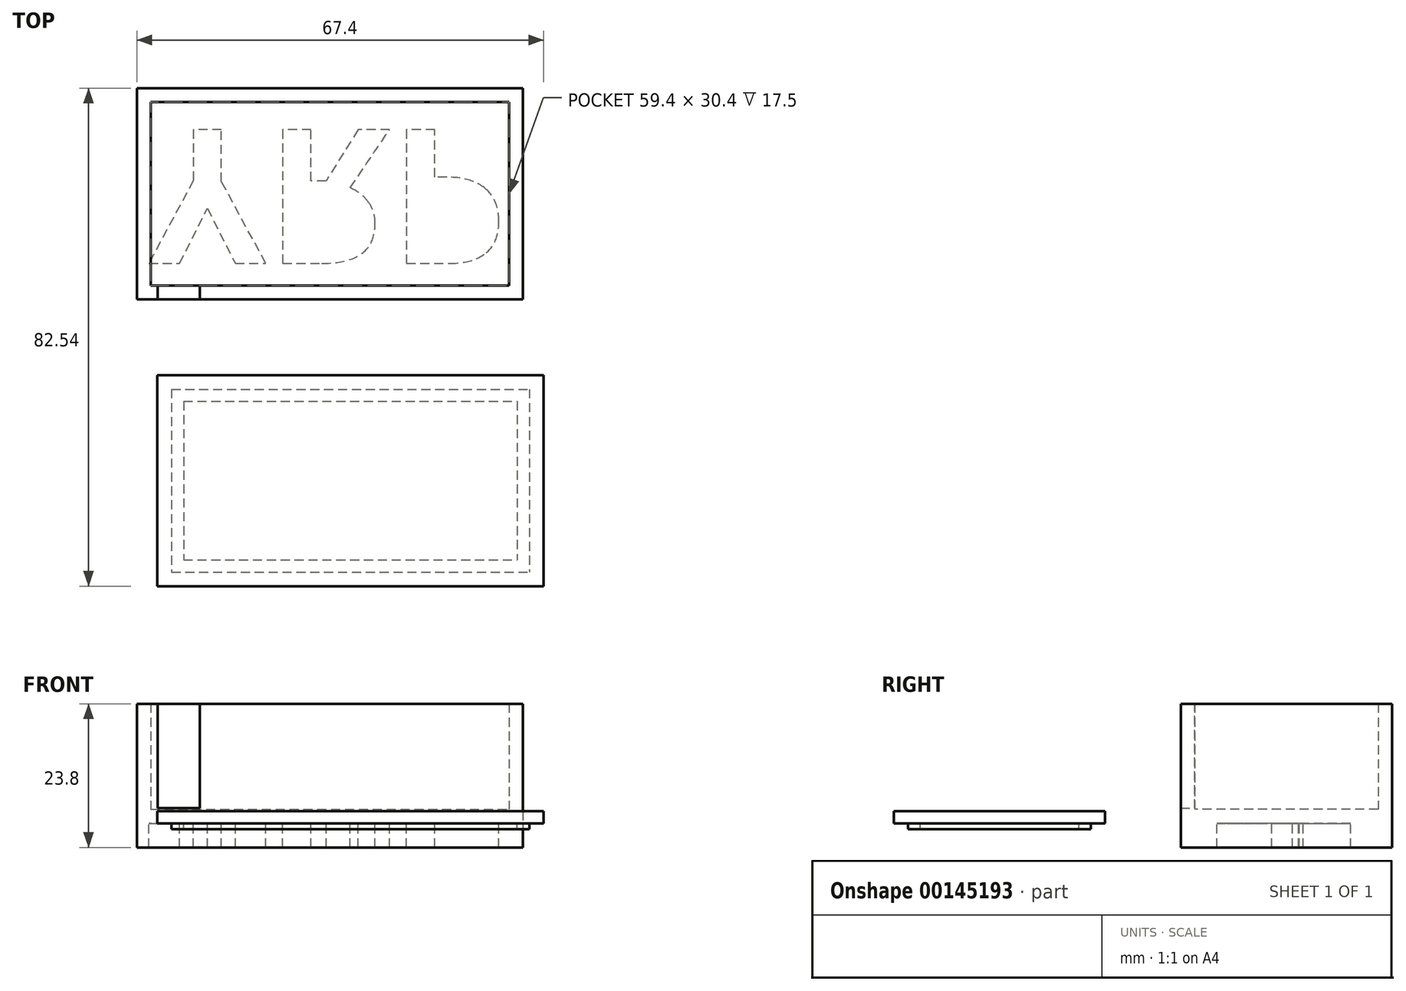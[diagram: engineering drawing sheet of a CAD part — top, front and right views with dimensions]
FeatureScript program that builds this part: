
annotation { "Feature Type Name" : "Feature", "Feature Type Description" : "" }
export const myFeature = defineFeature(function(context is Context, id is Id, definition is map)
    precondition{}
    {
        {
            var Q0;
            Q0=qCreatedBy(makeId("Top.planeOp"),FACE);
            var sketch = newSketch(context, id + "F0", { "sketchPlane" : qUnion([Q0])});
            skLineSegment(sketch, "E0.bottom", {"start": v(-34.01, 10.7) * mm, "end": v(29.99, 10.7) * mm});
            skLineSegment(sketch, "E0.top", {"start": v(-34.01, -24.3) * mm, "end": v(29.99, -24.3) * mm});
            skLineSegment(sketch, "E0.left", {"start": v(-34.01, 10.7) * mm, "end": v(-34.01, -24.3) * mm});
            skLineSegment(sketch, "E0.right", {"start": v(29.99, 10.7) * mm, "end": v(29.99, -24.3) * mm});
            skSolve(sketch);
        }
        {
            var Q0;
            Q0=makeQuery(id+"F0.imprint","IMPRINT",FACE,{"disambiguationData":[TD([[makeQuery(id+"F0.imprint","IMPRINT",EDGE,{"derivedFrom":sQuery(id+"F0.wireOp",EDGE,"E0.bottom")}),-1.0]])]});
            extrude(context, id + "F1", {"entities" : qUnion([Q0]), "depth" : 19.8 * mm});
        }
        {
            var Q0;
            Q0=makeQuery(id+"F1.opExtrude","CAP_FACE",FACE,{"disambiguationData":[OSD([sQuery(id+"F0.wireOp",EDGE,"E0.bottom"),sQuery(id+"F0.wireOp",EDGE,"E0.top"),sQuery(id+"F0.wireOp",EDGE,"E0.left"),sQuery(id+"F0.wireOp",EDGE,"E0.right")])],"isStart":false});
            shell(context, id + "F2", {"entities" : qUnion([Q0]), "thickness" : 2.3 * mm});
        }
        {
            var Q0;
            Q0=makeQuery(id+"F1.opExtrude","CAP_FACE",FACE,{"disambiguationData":[OSD([sQuery(id+"F0.wireOp",EDGE,"E0.bottom"),sQuery(id+"F0.wireOp",EDGE,"E0.top"),sQuery(id+"F0.wireOp",EDGE,"E0.left"),sQuery(id+"F0.wireOp",EDGE,"E0.right")])],"isStart":true});
            var sketch = newSketch(context, id + "F3", { "sketchPlane" : qUnion([Q0])});
            skText(sketch, "E1", { "text": "YRP", "fontName": "OpenSans-Bold.ttf"});
            const initialGuessF3  = {"E1": [-0.03201, -0.00384, 1, 0, 0.02236]};
            skSetInitialGuess(sketch, initialGuessF3);
            skSolve(sketch);
        }
        {
            var Q0;
            Q0=makeQuery(id+"F1.opExtrude","CAP_FACE",FACE,{"disambiguationData":[OSD([sQuery(id+"F0.wireOp",EDGE,"E0.bottom"),sQuery(id+"F0.wireOp",EDGE,"E0.top"),sQuery(id+"F0.wireOp",EDGE,"E0.left"),sQuery(id+"F0.wireOp",EDGE,"E0.right")])],"isStart":false});
            var sketch = newSketch(context, id + "F4", { "sketchPlane" : qUnion([Q0])});
            skLineSegment(sketch, "E2.bottom", {"start": v(-30.55, -24.3) * mm, "end": v(-23.55, -24.3) * mm});
            skLineSegment(sketch, "E2.top", {"start": v(-30.55, -22) * mm, "end": v(-23.55, -22) * mm});
            skLineSegment(sketch, "E2.left", {"start": v(-30.55, -24.3) * mm, "end": v(-30.55, -22) * mm});
            skLineSegment(sketch, "E2.right", {"start": v(-23.55, -24.3) * mm, "end": v(-23.55, -22) * mm});
            skSolve(sketch);
        }
        {
            var Q0;
            Q0=makeQuery(id+"F4.imprint","IMPRINT",FACE,{"disambiguationData":[TD([[makeQuery(id+"F4.imprint","IMPRINT",EDGE,{"derivedFrom":sQuery(id+"F4.wireOp",EDGE,"E2.bottom")}),1.0]])]});
            extrude(context, id + "F5", {"entities" : qUnion([Q0]), "operationType" : NewBodyOperationType.REMOVE, "oppositeDirection" : true, "depth" : 17.3 * mm});
        }
        {
            var Q0;
            Q0=makeQuery(id+"F3.imprint","IMPRINT",FACE,{"disambiguationData":[TD([[makeQuery(id+"F3.imprint","IMPRINT",EDGE,{"derivedFrom":sQuery(id+"F3.wireOp",EDGE,"E1.sketch_text.stroke-0")}),1.0]])]});
            extrude(context, id + "F6", {"entities" : qUnion([Q0]), "operationType" : NewBodyOperationType.ADD, "depth" : 4 * mm});
        }
        {
            var Q0;
            Q0=qCreatedBy(makeId("Top.planeOp"),FACE);
            var sketch = newSketch(context, id + "F7", { "sketchPlane" : qUnion([Q0])});
            skLineSegment(sketch, "E3.bottom", {"start": v(-30.61, -36.84) * mm, "end": v(33.39, -36.84) * mm});
            skLineSegment(sketch, "E3.top", {"start": v(-30.61, -71.84) * mm, "end": v(33.39, -71.84) * mm});
            skLineSegment(sketch, "E3.left", {"start": v(-30.61, -36.84) * mm, "end": v(-30.61, -71.84) * mm});
            skLineSegment(sketch, "E3.right", {"start": v(33.39, -36.84) * mm, "end": v(33.39, -71.84) * mm});
            skSolve(sketch);
        }
        {
            var Q0;
            Q0=makeQuery(id+"F7.imprint","IMPRINT",FACE,{"disambiguationData":[TD([[makeQuery(id+"F7.imprint","IMPRINT",EDGE,{"derivedFrom":sQuery(id+"F7.wireOp",EDGE,"E3.bottom")}),-1.0]])]});
            var sketch = newSketch(context, id + "F8", { "sketchPlane" : qUnion([Q0])});
            skLineSegment(sketch, "E4.bottom", {"start": v(-28.26, -39.2) * mm, "end": v(31.04, -39.2) * mm});
            skLineSegment(sketch, "E4.top", {"start": v(-28.26, -69.5) * mm, "end": v(31.04, -69.5) * mm});
            skLineSegment(sketch, "E4.left", {"start": v(-28.26, -39.2) * mm, "end": v(-28.26, -69.5) * mm});
            skLineSegment(sketch, "E4.right", {"start": v(31.04, -39.2) * mm, "end": v(31.04, -69.5) * mm});
            skLineSegment(sketch, "E5.bottom", {"start": v(-26.26, -41.2) * mm, "end": v(29.04, -41.2) * mm});
            skLineSegment(sketch, "E5.top", {"start": v(-26.26, -67.5) * mm, "end": v(29.04, -67.5) * mm});
            skLineSegment(sketch, "E5.left", {"start": v(-26.26, -41.2) * mm, "end": v(-26.26, -67.5) * mm});
            skLineSegment(sketch, "E5.right", {"start": v(29.04, -41.2) * mm, "end": v(29.04, -67.5) * mm});
            skSolve(sketch);
        }
        {
            var Q0;
            Q0 = qSketchRegion(id + "F7", true);
            extrude(context, id + "F9", {"entities" : qUnion([Q0]), "depth" : 2 * mm});
        }
        {
            var Q0;
            Q0 = qSketchRegion(id + "F8", true);
            extrude(context, id + "F10", {"entities" : qUnion([Q0]), "operationType" : NewBodyOperationType.ADD, "oppositeDirection" : true, "depth" : 1 * mm});
        }
    });
